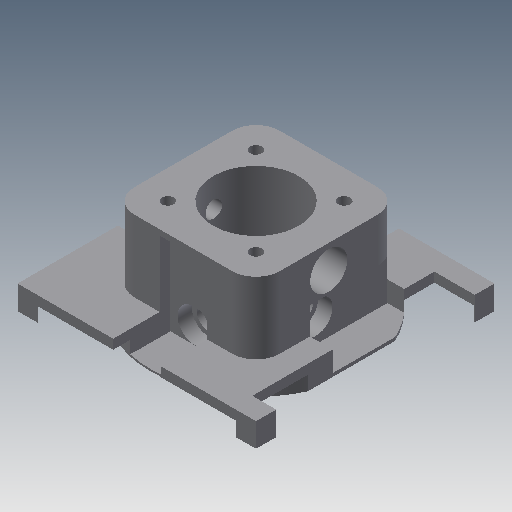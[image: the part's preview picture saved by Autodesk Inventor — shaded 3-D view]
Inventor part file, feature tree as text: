
AUTODESK INVENTOR PART (.ipt)
format: ipt  version: 2018 (Build 220112000, 112)  size: 412,672 bytes
history: native  units: in
note: dims shown in document units (in); Inventor stores cm internally (conversion verified against a paired STEP export)
features: extrude x15, hole x12, sketch x7, fillet x4
ambient origin geometry x8: Origin, YZ Plane, XZ Plane, XY Plane, X Axis, Y Axis, Z Axis, Center Point
bodies: Solid1 (feature_tree)
feature tree (38):
  extrude  "Extrusion1"  Depth=3.1496in
  extrude  "Extrusion2"  Depth=0.5906in TaperAngle=0.0deg
  hole  "Hole1"  [1 undecoded]
  hole  "Hole10"  [1 undecoded]
  hole  "Hole11"  [1 undecoded]
  extrude  "Extrusion11"  Depth=0.7283in TaperAngle=0.0deg
  hole  "Hole12"  [1 undecoded]
  extrude  "Extrusion13"  Depth=0.7283in TaperAngle=0.0deg
  hole  "Hole14"  [1 undecoded]
  extrude  "Extrusion14"  Depth=0.3937in
  hole  "Hole15"  [1 undecoded]
  extrude  "Extrusion15"  Depth=0.1969in TaperAngle=0.0deg
  hole  "Hole16"  [1 undecoded]
  extrude  "Extrusion16"  Depth=0.7283in
  extrude  "Extrusion17"  Depth=0.1969in TaperAngle=0.0deg
  extrude  "Extrusion18"  Depth=0.3937in
  hole  "Hole24"  [1 undecoded]
  extrude  "Extrusion19"  Depth=0.1969in TaperAngle=0.0deg
  extrude  "Extrusion20"  Depth=0.2756in
  extrude  "Extrusion22"  Depth=0.3937in
  extrude  "Extrusion23"  Depth=0.3937in
  extrude  "Extrusion24"  Depth=0.1969in TaperAngle=0.0deg
  fillet  "Fillet9"  Radius=1.5748in
  fillet  "Fillet10"  Radius=1.1811in
  fillet  "Fillet11"  Radius=1.7323in
  fillet  "Fillet12"  Radius=2.5591in
  extrude  "Extrusion25"  Depth=0.1181in TaperAngle=0.0deg
  hole  "Hole26"  [1 undecoded]
  hole  "Hole27"  [1 undecoded]
  hole  "Hole28"  [1 undecoded]
  hole  "Hole29"  [1 undecoded]
  sketch  "Sketch16"  dims[d0=3.1496in d1=3.1496in]
  sketch  "Sketch17"  dims[d9=0.1969in d10=0.0in d12=0.5906in d13=0.0in]
  sketch  "Sketch19"  dims[d14=1.5748in d15=1.5748in d16=0.7087in d17=0.2356in d18=0.748in d19=0.0787in d20=30.0deg d21=0.9843in d22=0.0in]
  sketch  "Sketch20"  dims[d144=0.3543in d145=0.7874in d146=0.1378in d147=0.2362in d148=0.1575in d149=0.0787in d150=90.0deg d151=0.315in d152=0.8108in]
  sketch  "Sketch23"  dims[d153=0.7874in d154=0.3937in d155=0.3071in d156=0.2362in d157=0.1575in d158=0.0787in d159=90.0deg d160=0.315in d161=0.8108in d162=0.2756in d163=0.0in]
  sketch  "Sketch24"  dims[d164=0.1535in d414=0.0394in d166=0.1969in d167=0.2362in d168=0.2756in d169=0.1181in d170=90.0deg d171=0.3937in d172=0.0in d173=0.3937in]
  sketch  "Sketch25"  dims[d174=0.7283in d189=0.5906in d191=0.7283in d192=0.3937in d194=0.0in d195=0.2756in d196=0.5906in d413=0.0394in d358=0.1535in d199=0.1969in d200=0.2362in d201=0.2756in d202=0.1181in d203=90.0deg d204=0.2756in d205=0.0in d207=0.7283in d208=0.3937in d210=0.0in d211=0.2756in d212=0.1378in d213=0.1969in d214=0.1969in d215=0.2362in d216=0.2756in d217=0.1181in d218=90.0deg d219=0.3937in d220=0.0in d221=0.7283in d222=0.3937in d224=0.0in d225=0.2756in d226=0.1378in d227=0.1969in d228=0.1969in d229=0.2362in d230=0.2756in d231=0.1181in d232=90.0deg d233=0.3937in d234=0.0in d275=0.3937in d276=0.7283in d277=0.1969in d278=0.0in d279=0.3937in d280=0.7283in d281=0.1969in d282=0.0in d302=0.3937in d303=0.3937in d304=0.1811in d305=0.0in d317=0.2756in d318=0.2756in d319=0.1969in d320=0.2362in d321=0.3543in d322=0.0787in d323=90.0deg d324=0.315in d325=0.8108in d326=0.3937in d327=0.3937in d328=0.1811in d329=0.0in d330=1.5748in d333=1.1811in d334=1.7323in d335=2.5591in d338=0.1181in d339=0.0in d355=0.0787in d356=0.0in d357=1.2008in d359=1.2008in d360=0.5906in d361=0.0in d362=1.9685in d363=1.9685in d364=0.7874in d365=0.0in d366=0.1969in d367=0.1969in d368=0.1969in d369=0.1969in d370=0.3937in d371=0.0in d374=0.2362in d375=0.2362in d376=0.0984in d377=0.2362in d378=0.1575in d379=0.0787in d380=90.0deg d381=0.1969in d382=0.8108in d383=0.2362in d384=0.2362in d385=0.0984in d386=0.2362in d387=0.1575in d388=0.0787in d389=90.0deg d390=0.1969in d391=0.8108in d392=0.2362in d393=0.2362in d394=0.0984in d395=0.2362in d396=0.1575in d397=0.0787in d398=90.0deg d399=0.1969in d400=0.8108in d401=0.2362in d402=0.2362in d403=0.0984in d404=0.2362in d405=0.1575in d406=0.0787in d407=90.0deg d408=0.1969in d409=0.8108in d410=0.6299in d411=0.0157in d412=0.0157in]
note: 12 required parameter values undecoded (feature->parameter linkage not recoverable at this tier; creation-order binding heuristic only, values carry confidence <= 0.55)
